# Revit family: Apollo Zero
name_source: partatom
category: Lighting Fixtures
units: mm (PartAtom-declared; Revit-internal decimal feet)

## family parameters
Always vertical = Yes
Cut with Voids When Loaded = No
Host = Ceiling
Light Source = Yes
OmniClass Number = 23.80.70.11
OmniClass Title = Luminaries for Internal Lighting
Part Type = Normal
Room Calculation Point = No
Round Connector Dimension = Use Diameter
Shared = No

## types (1)
- Apollo Zero
    ArticleNumber = 492114
    AssetType = Movable
    Brand = Pholc
    Cable Length (default) = 700 mm  [stored 2.29659 ft]
    Category = Pendants
    Class = Class 2
    Color = Aluminium/Black
    Color Filter = 16777215
    Default Elevation = 0 mm  [stored 0 ft]
    Dimming Lamp Color Temperature Shift = <None>
    IFC classification = Light Fixture
    IP_Code = IP20
    Light Source Symbol Length = 3048 mm  [stored 10 ft]
    LightFixtureMountingType = Pendants
    LightFixturePlacingType = Ceiling
    Lightsource included = No
    Lightsource type = Gu10
    Manufacturer = Pholc
    Manufacturer Name = Pholc
    ManufacturerName = Pholc
    ManufacturerURL = https://www.pholc.se
    Material = Aluminium/Black
    Max watt = 15
    Model = 492114
    Model Name = Apollo Zero
    ModelNumber = 492114
    ModelReference = Apollo Zero
    NBS Reference Description = General purpose luminaires
    NBSReference = 90-60-50/405
    Name = Apollo Zero
    Nominal Height = 95 mm
    Nominal Length = 125 mm  [stored 0.410105 ft]
    Nominal Width = 125 mm  [stored 0.410105 ft]
    NominalCurrent = 0 A
    NominalVoltage = 0 V
    Shape = Cone
    Size = 125
    Socket = Gu10
    Spot Beam Angle = 30.00°
    Spot Field Angle = 90.00°
    Surface Material = Aluminum Pholc
    Tilt Angle = 90.00°
    TotalWattage = 15 W
    URL = https://www.pholc.se
https://www.pholc.se
    Uniclass2015Description = Pendant luminaires
    Uniclass2015Reference = Pr_70_70_48_62
    VisualHusRef = Pholc_Id083

note: [stored X ft] marks values corroborated as IEEE doubles in the binary element streams (Revit-internal decimal feet)

## geometry (parser evidence)
native form markers: Sweep x2
no freeform markers — native parametric forms only
